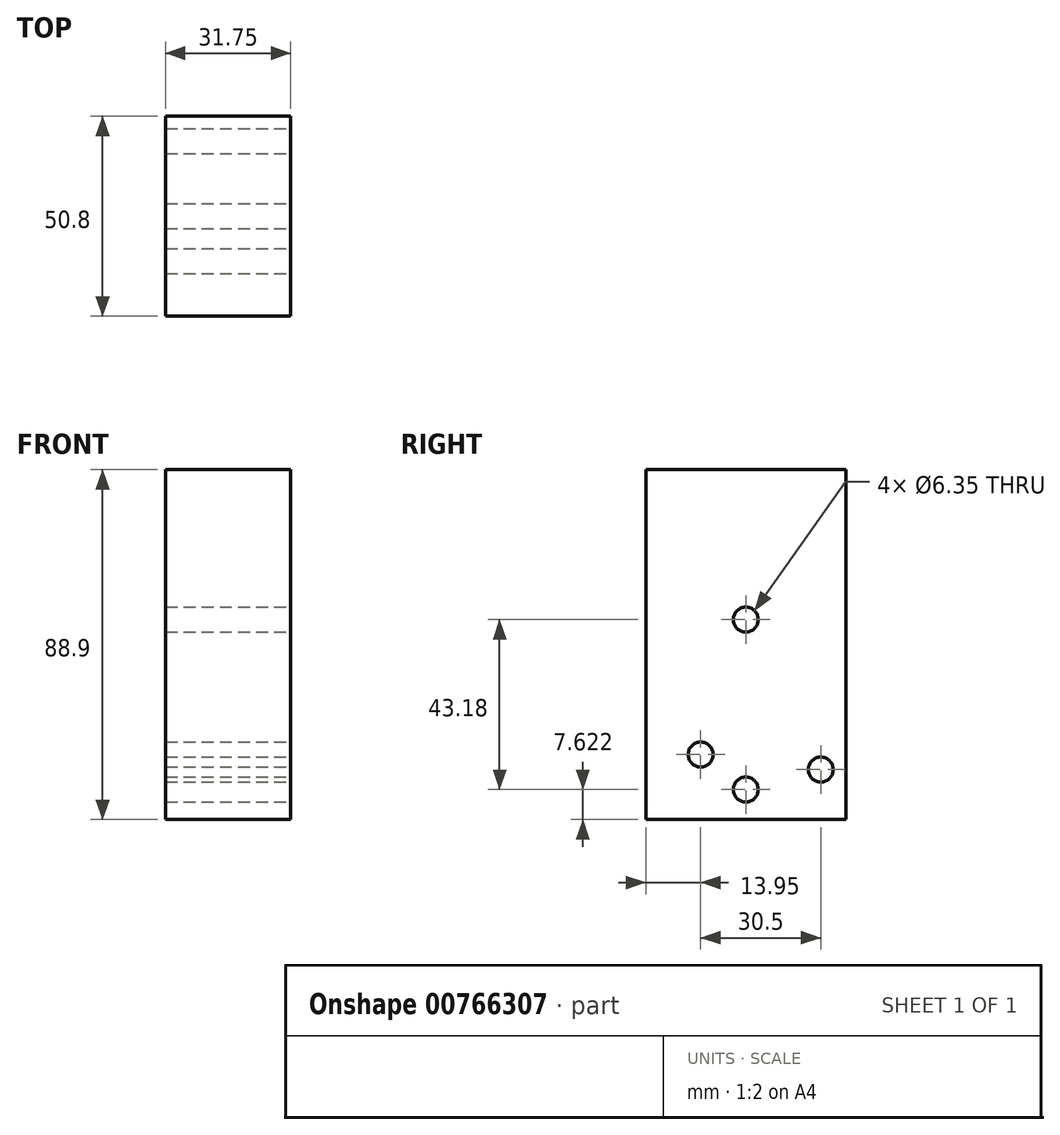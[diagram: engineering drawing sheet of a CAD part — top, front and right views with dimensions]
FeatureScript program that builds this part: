
annotation { "Feature Type Name" : "Feature", "Feature Type Description" : "" }
export const myFeature = defineFeature(function(context is Context, id is Id, definition is map)
    precondition{}
    {
        {
            var Q0;
            Q0=qCreatedBy(makeId("Front.planeOp"),FACE);
            var sketch = newSketch(context, id + "F0", { "sketchPlane" : qUnion([Q0])});
            skLineSegment(sketch, "E0.bottom", {"start": v(-36.6, 24.67) * mm, "end": v(-68.34, 24.67) * mm});
            skLineSegment(sketch, "E0.top", {"start": v(-36.6, 113.57) * mm, "end": v(-68.34, 113.57) * mm});
            skLineSegment(sketch, "E0.left", {"start": v(-36.6, 24.67) * mm, "end": v(-36.6, 113.57) * mm});
            skLineSegment(sketch, "E0.right", {"start": v(-68.34, 24.67) * mm, "end": v(-68.34, 113.57) * mm});
            skSolve(sketch);
        }
        {
            var Q0;
            Q0=makeQuery(id+"F0.imprint","IMPRINT",FACE,{"disambiguationData":[TD([[makeQuery(id+"F0.imprint","IMPRINT",EDGE,{"derivedFrom":sQuery(id+"F0.wireOp",EDGE,"E0.bottom")}),-1.0]])]});
            extrude(context, id + "F1", {"entities" : qUnion([Q0]), "depth" : 50.8 * mm, "offsetDistance" : 25.4 * mm});
        }
        {
            var Q0;
            Q0=makeQuery(id+"F1.opExtrude","SWEPT_FACE",FACE,{"disambiguationData":[OSD([sQuery(id+"F0.wireOp",EDGE,"E0.left")])]});
            var sketch = newSketch(context, id + "F2", { "sketchPlane" : qUnion([Q0])});
            skCircle(sketch, "E1", {"center": v(-25.4, 75.47) * mm, "radius": 3.18 * mm});
            skCircle(sketch, "E2", {"center": v(-25.4, 32.3) * mm, "radius": 3.18 * mm});
            skCircle(sketch, "E3", {"center": v(-6.35, 37.37) * mm, "radius": 3.18 * mm});
            skSolve(sketch);
        }
        {
            var Q0;
            Q0 = qSketchRegion(id + "F2", true);
            extrude(context, id + "F3", {"entities" : qUnion([Q0]), "operationType" : NewBodyOperationType.REMOVE, "oppositeDirection" : true, "depth" : 76.2 * mm, "offsetDistance" : 25.4 * mm});
        }
        {
            var Q0;
            Q0=makeQuery(id+"F1.opExtrude","SWEPT_FACE",FACE,{"disambiguationData":[OSD([sQuery(id+"F0.wireOp",EDGE,"E0.left")])]});
            var sketch = newSketch(context, id + "F4", { "sketchPlane" : qUnion([Q0])});
            skCircle(sketch, "E4", {"center": v(-36.85, 41.2) * mm, "radius": 3.18 * mm});
            skSolve(sketch);
        }
        {
            var Q0;
            Q0 = qSketchRegion(id + "F4", true);
            extrude(context, id + "F5", {"entities" : qUnion([Q0]), "operationType" : NewBodyOperationType.REMOVE, "oppositeDirection" : true, "depth" : 25.4 * mm, "offsetDistance" : 25.4 * mm});
        }
        {
            var Q0;
            Q0 = qSketchRegion(id + "F4", true);
            extrude(context, id + "F6", {"entities" : qUnion([Q0]), "operationType" : NewBodyOperationType.REMOVE, "oppositeDirection" : true, "depth" : 38.1 * mm, "offsetDistance" : 25.4 * mm});
        }
    });
